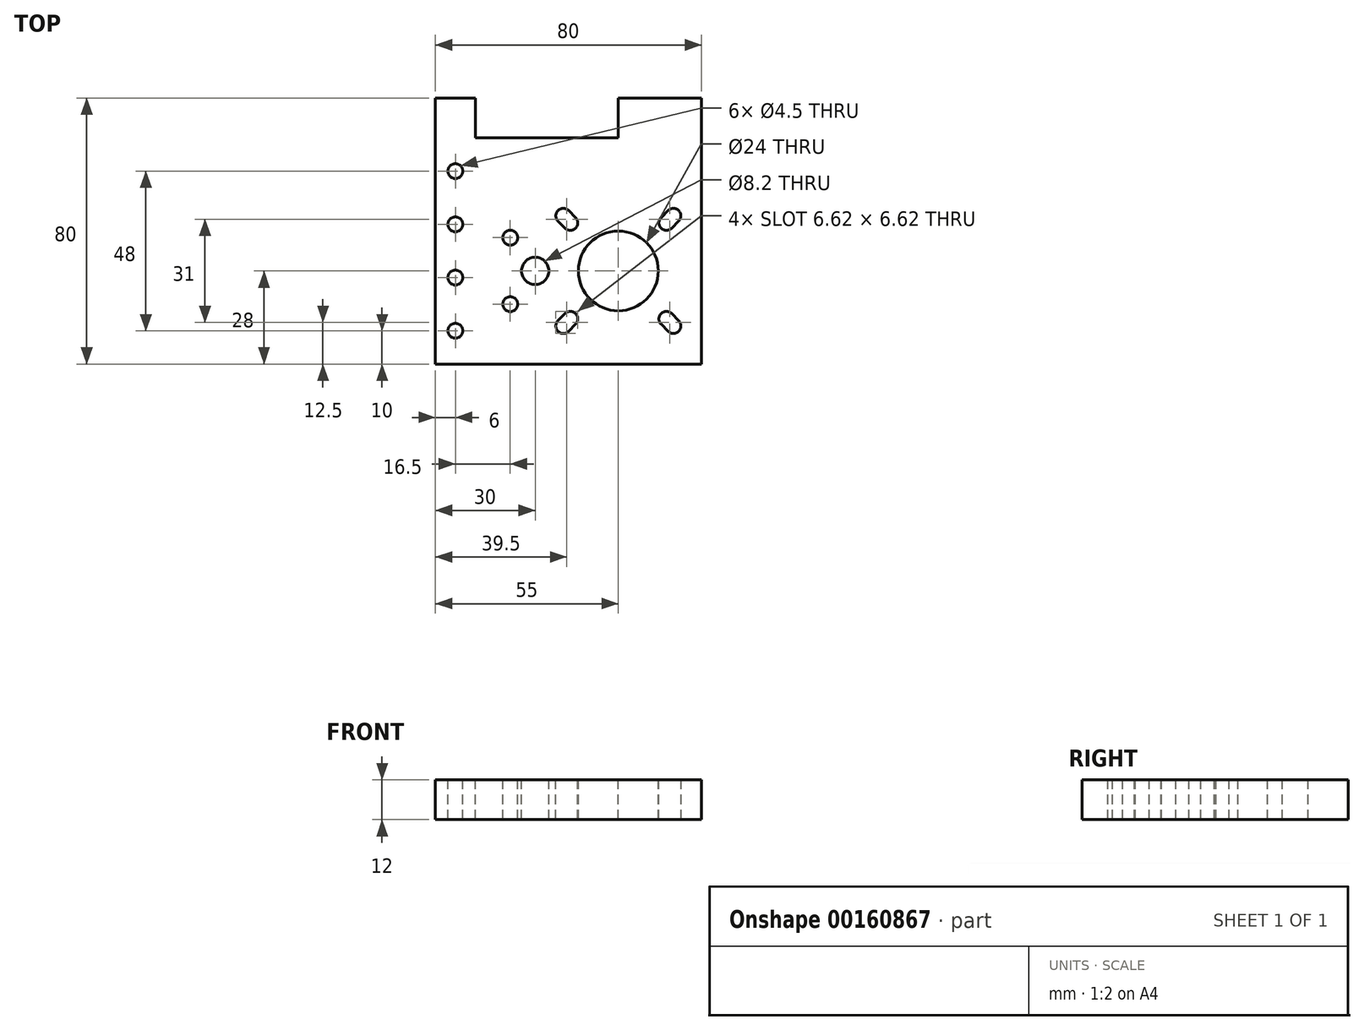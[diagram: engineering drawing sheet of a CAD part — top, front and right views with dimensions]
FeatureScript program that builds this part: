
annotation { "Feature Type Name" : "Feature", "Feature Type Description" : "" }
export const myFeature = defineFeature(function(context is Context, id is Id, definition is map)
    precondition{}
    {
        {
            var Q0;
            Q0=qCreatedBy(makeId("Top.planeOp"),FACE);
            var sketch = newSketch(context, id + "F0", { "sketchPlane" : qUnion([Q0])});
            skLineSegment(sketch, "E0.top", {"start": v(-40, -40) * mm, "end": v(40, -40) * mm});
            skLineSegment(sketch, "E0.left", {"start": v(-40, 40) * mm, "end": v(-40, -40) * mm});
            skLineSegment(sketch, "E0.right", {"start": v(40, 40) * mm, "end": v(40, -40) * mm});
            skPoint(sketch, "E1", {"position": v(40, 0) * mm});
            skPoint(sketch, "E2", {"position": v(0, -40) * mm});
            skLineSegment(sketch, "E3", {"start": v(40, 40) * mm, "end": v(15, 40) * mm});
            skLineSegment(sketch, "E4", {"start": v(15, 40) * mm, "end": v(15, 28) * mm});
            skLineSegment(sketch, "E5", {"start": v(15, 28) * mm, "end": v(-28, 28) * mm});
            skLineSegment(sketch, "E6", {"start": v(-28, 28) * mm, "end": v(-28, 40) * mm});
            skLineSegment(sketch, "E7", {"start": v(-28, 40) * mm, "end": v(-40, 40) * mm});
            skCircle(sketch, "E8", {"center": v(15, -12) * mm, "radius": 12 * mm});
            skCircle(sketch, "E9", {"center": v(-10, -12) * mm, "radius": 4.1 * mm});
            skCircle(sketch, "E10", {"center": v(-17.5, -22) * mm, "radius": 2.25 * mm});
            skLineSegment(sketch, "E11", {"start": v(-10, -12) * mm, "end": v(-22.14, -12) * mm, "construction": true});
            skCircle(sketch, "E12.MirrorC", {"center": v(-17.5, -2) * mm, "radius": 2.25 * mm});
            skCircle(sketch, "E13", {"center": v(-34, -30) * mm, "radius": 2.25 * mm});
            skCircle(sketch, "E14.1.0.0", {"center": v(-34, -14) * mm, "radius": 2.25 * mm});
            skCircle(sketch, "E14.2.0.0", {"center": v(-34, 2) * mm, "radius": 2.25 * mm});
            skLineSegment(sketch, "E14.direction1", {"start": v(-34, -30) * mm, "end": v(-34, -14) * mm, "construction": true});
            skPoint(sketch, "E15", {"position": v(30.5, 3.5) * mm});
            skLineSegment(sketch, "E16", {"start": v(3, -12) * mm, "end": v(27, -12) * mm, "construction": true});
            skLineSegment(sketch, "E17", {"start": v(15, -24) * mm, "end": v(15, 0) * mm, "construction": true});
            skCircle(sketch, "E18.0.3.0", {"center": v(-34, 18) * mm, "radius": 2.25 * mm});
            skLineSegment(sketch, "E19", {"start": v(31.56, 4.56) * mm, "end": v(29.44, 2.44) * mm, "construction": true});
            skCircle(sketch, "E20", {"center": v(31.56, 4.56) * mm, "radius": 2.25 * mm});
            skCircle(sketch, "E21", {"center": v(29.44, 2.44) * mm, "radius": 2.25 * mm});
            skLineSegment(sketch, "E22", {"start": v(33.15, 2.97) * mm, "end": v(31.03, 0.85) * mm});
            skLineSegment(sketch, "E23.MirrorCS", {"start": v(29.97, 6.15) * mm, "end": v(27.85, 4.03) * mm});
            skLineSegment(sketch, "E24.MirrorCS", {"start": v(0.03, 6.15) * mm, "end": v(2.15, 4.03) * mm});
            skCircle(sketch, "E25.MirrorC", {"center": v(0.56, 2.44) * mm, "radius": 2.25 * mm});
            skCircle(sketch, "E26.MirrorC", {"center": v(-1.56, 4.56) * mm, "radius": 2.25 * mm});
            skLineSegment(sketch, "E27.MirrorCS", {"start": v(-3.15, 2.97) * mm, "end": v(-1.03, 0.85) * mm});
            skCircle(sketch, "E28.MirrorC", {"center": v(0.56, -26.44) * mm, "radius": 2.25 * mm});
            skCircle(sketch, "E29.MirrorC", {"center": v(-1.56, -28.56) * mm, "radius": 2.25 * mm});
            skLineSegment(sketch, "E30.MirrorCS", {"start": v(0.03, -30.15) * mm, "end": v(2.15, -28.03) * mm});
            skLineSegment(sketch, "E31.MirrorCS", {"start": v(-3.15, -26.97) * mm, "end": v(-1.03, -24.85) * mm});
            skLineSegment(sketch, "E32.MirrorCS", {"start": v(29.97, -30.15) * mm, "end": v(27.85, -28.03) * mm});
            skCircle(sketch, "E33.MirrorC", {"center": v(29.44, -26.44) * mm, "radius": 2.25 * mm});
            skCircle(sketch, "E34.MirrorC", {"center": v(31.56, -28.56) * mm, "radius": 2.25 * mm});
            skLineSegment(sketch, "E35.MirrorCS", {"start": v(33.15, -26.97) * mm, "end": v(31.03, -24.85) * mm});
            skSolve(sketch);
        }
        {
            var Q0;
            Q0 = qSketchRegion(id + "F0", true);
            extrude(context, id + "F1", {"entities" : qUnion([Q0]), "oppositeDirection" : true, "depth" : 12 * mm});
        }
    });
